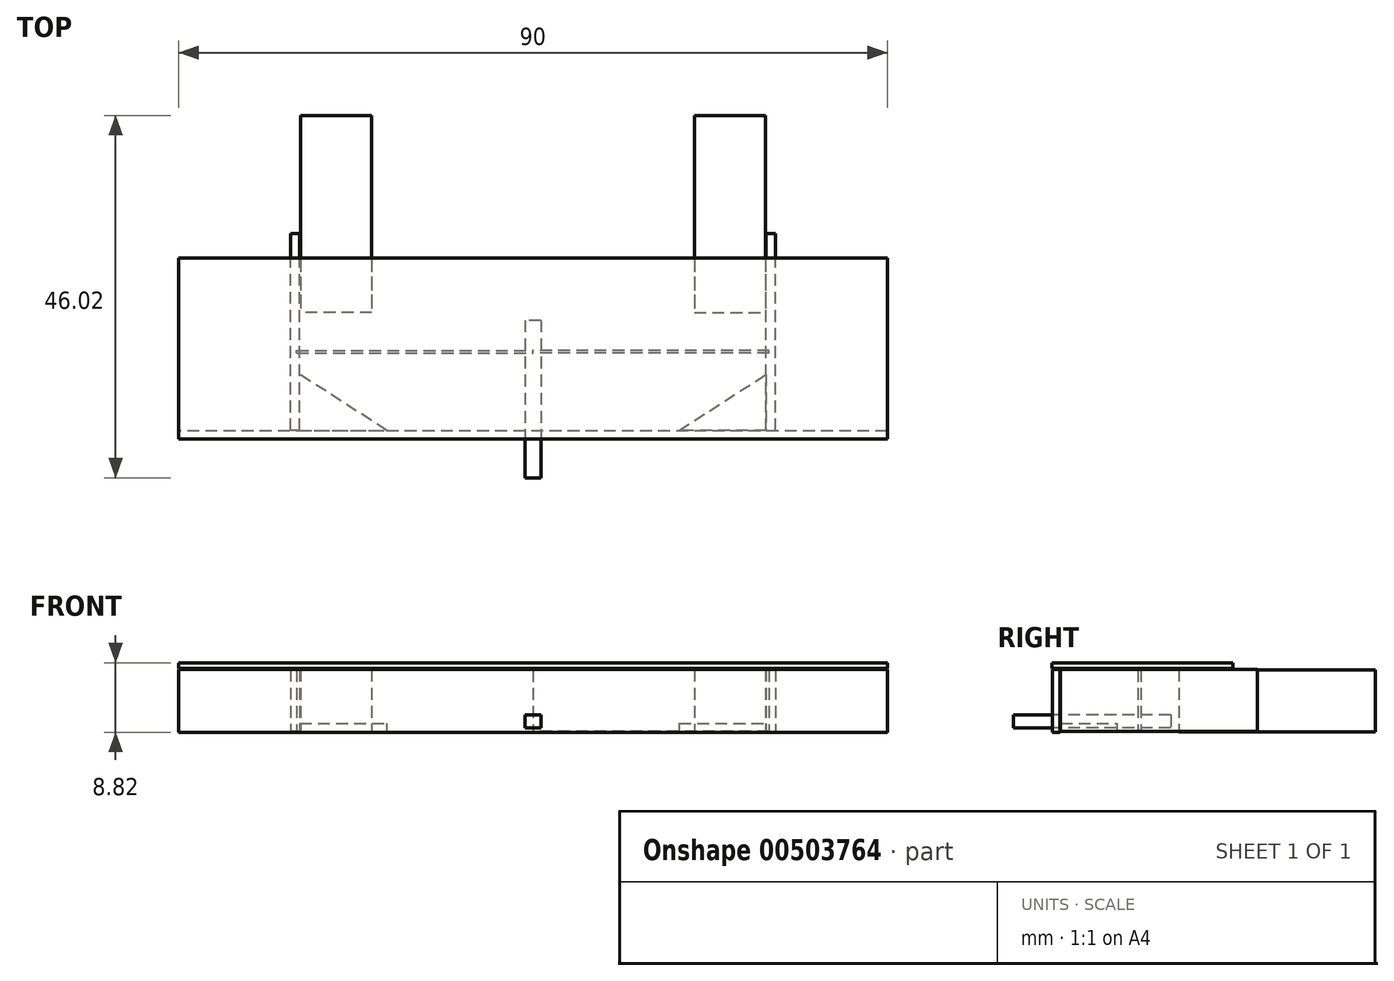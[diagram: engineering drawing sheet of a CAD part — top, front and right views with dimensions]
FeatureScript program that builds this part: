
annotation { "Feature Type Name" : "Feature", "Feature Type Description" : "" }
export const myFeature = defineFeature(function(context is Context, id is Id, definition is map)
    precondition{}
    {
        {
            var Q0;
            Q0=qCreatedBy(makeId("Front.planeOp"),FACE);
            var sketch = newSketch(context, id + "F0", { "sketchPlane" : qUnion([Q0])});
            skLineSegment(sketch, "E0.bottom", {"start": v(-20.5, 3.93) * mm, "end": v(-29.5, 3.93) * mm});
            skLineSegment(sketch, "E0.top", {"start": v(-20.5, -3.93) * mm, "end": v(-29.5, -3.93) * mm});
            skLineSegment(sketch, "E0.left", {"start": v(-20.5, 3.93) * mm, "end": v(-20.5, -3.93) * mm});
            skLineSegment(sketch, "E0.right", {"start": v(-29.5, 3.93) * mm, "end": v(-29.5, -3.93) * mm});
            skPoint(sketch, "E0.middle", {"position": v(-25, 0) * mm});
            skPoint(sketch, "E1.MirrorP", {"position": v(25, 0) * mm});
            skLineSegment(sketch, "E2.MirrorCS", {"start": v(20.5, 3.93) * mm, "end": v(20.5, -3.93) * mm});
            skLineSegment(sketch, "E3.MirrorCS", {"start": v(20.5, 3.93) * mm, "end": v(29.5, 3.93) * mm});
            skLineSegment(sketch, "E4.MirrorCS", {"start": v(29.5, 3.93) * mm, "end": v(29.5, -3.93) * mm});
            skLineSegment(sketch, "E5.MirrorCS", {"start": v(20.5, -3.93) * mm, "end": v(29.5, -3.93) * mm});
            skSolve(sketch);
        }
        {
            var Q0;
            Q0=makeQuery(id+"F0.imprint","IMPRINT",FACE,{"disambiguationData":[TD([[makeQuery(id+"F0.imprint","IMPRINT",EDGE,{"derivedFrom":sQuery(id+"F0.wireOp",EDGE,"E0.bottom")}),1.0]])]});
            var Q1;
            Q1=makeQuery(id+"F0.imprint","IMPRINT",FACE,{"disambiguationData":[TD([[makeQuery(id+"F0.imprint","IMPRINT",EDGE,{"derivedFrom":sQuery(id+"F0.wireOp",EDGE,"E2.MirrorCS")}),1.0]])]});
            extrude(context, id + "F1", {"entities" : qUnion([Q0, Q1]), "oppositeDirection" : true, "depth" : 25 * mm});
        }
        {
            var Q0;
            Q0=qCreatedBy(makeId("Front.planeOp"),FACE);
            var sketch = newSketch(context, id + "F2", { "sketchPlane" : qUnion([Q0])});
            skLineSegment(sketch, "E6.bottom", {"start": v(-29.62, 3.95) * mm, "end": v(-30.78, 3.95) * mm});
            skLineSegment(sketch, "E6.top", {"start": v(-29.62, -3.88) * mm, "end": v(-30.78, -3.88) * mm});
            skLineSegment(sketch, "E6.left", {"start": v(-29.62, 3.95) * mm, "end": v(-29.62, -3.88) * mm});
            skLineSegment(sketch, "E6.right", {"start": v(-30.78, 3.95) * mm, "end": v(-30.78, -3.88) * mm});
            skLineSegment(sketch, "E7.MirrorCS", {"start": v(29.62, 3.95) * mm, "end": v(29.62, -3.88) * mm});
            skLineSegment(sketch, "E8.MirrorCS", {"start": v(30.78, 3.95) * mm, "end": v(30.78, -3.88) * mm});
            skLineSegment(sketch, "E9.MirrorCS", {"start": v(29.62, -3.88) * mm, "end": v(30.78, -3.88) * mm});
            skLineSegment(sketch, "E10.MirrorCS", {"start": v(29.62, 3.95) * mm, "end": v(30.78, 3.95) * mm});
            skSolve(sketch);
        }
        {
            var Q0;
            Q0 = qSketchRegion(id + "F2", true);
            extrude(context, id + "F3", {"entities" : qUnion([Q0]), "depth" : 15 * mm});
        }
        {
            var Q0;
            Q0=makeQuery(id+"F3.opExtrude","CAP_FACE",FACE,{"disambiguationData":[OSD([sQuery(id+"F2.wireOp",EDGE,"E6.bottom"),sQuery(id+"F2.wireOp",EDGE,"E6.top"),sQuery(id+"F2.wireOp",EDGE,"E6.left"),sQuery(id+"F2.wireOp",EDGE,"E6.right")])],"isStart":true});
            extrude(context, id + "F4", {"entities" : qUnion([Q0]), "operationType" : NewBodyOperationType.ADD, "depth" : 10 * mm});
        }
        {
            var Q0;
            Q0=makeQuery(id+"F3.opExtrude","CAP_FACE",FACE,{"disambiguationData":[OSD([sQuery(id+"F2.wireOp",EDGE,"E7.MirrorCS"),sQuery(id+"F2.wireOp",EDGE,"E8.MirrorCS"),sQuery(id+"F2.wireOp",EDGE,"E9.MirrorCS"),sQuery(id+"F2.wireOp",EDGE,"E10.MirrorCS")])],"isStart":true});
            extrude(context, id + "F5", {"entities" : qUnion([Q0]), "operationType" : NewBodyOperationType.ADD, "depth" : 10 * mm});
        }
        {
            var Q0;
            Q0=qCreatedBy(makeId("Right.planeOp"),FACE);
            var sketch = newSketch(context, id + "F6", { "sketchPlane" : qUnion([Q0])});
            skLineSegment(sketch, "E11.bottom", {"start": v(-15.08, 3.97) * mm, "end": v(-16.02, 3.97) * mm});
            skLineSegment(sketch, "E11.top", {"start": v(-15.08, -4) * mm, "end": v(-16.02, -4) * mm});
            skLineSegment(sketch, "E11.left", {"start": v(-15.08, 3.97) * mm, "end": v(-15.08, -4) * mm});
            skLineSegment(sketch, "E11.right", {"start": v(-16.02, 3.97) * mm, "end": v(-16.02, -4) * mm});
            skSolve(sketch);
        }
        {
            var Q0;
            Q0=makeQuery(id+"F6.imprint","IMPRINT",FACE,{"disambiguationData":[TD([[makeQuery(id+"F6.imprint","IMPRINT",EDGE,{"derivedFrom":sQuery(id+"F6.wireOp",EDGE,"E11.bottom")}),1.0]])]});
            extrude(context, id + "F7", {"entities" : qUnion([Q0]), "depth" : 45 * mm});
        }
        {
            var Q0;
            Q0=makeQuery(id+"F7.opExtrude","CAP_FACE",FACE,{"disambiguationData":[OSD([sQuery(id+"F6.wireOp",EDGE,"E11.bottom"),sQuery(id+"F6.wireOp",EDGE,"E11.top"),sQuery(id+"F6.wireOp",EDGE,"E11.left"),sQuery(id+"F6.wireOp",EDGE,"E11.right")])],"isStart":true});
            extrude(context, id + "F8", {"entities" : qUnion([Q0]), "operationType" : NewBodyOperationType.ADD, "depth" : 45 * mm});
        }
        {
            var Q0;
            Q0=qCreatedBy(makeId("Right.planeOp"),FACE);
            var sketch = newSketch(context, id + "F9", { "sketchPlane" : qUnion([Q0])});
            skLineSegment(sketch, "E12.bottom", {"start": v(-16.1, 4.1) * mm, "end": v(6.88, 4.1) * mm});
            skLineSegment(sketch, "E12.top", {"start": v(-16.1, 4.81) * mm, "end": v(6.88, 4.81) * mm});
            skLineSegment(sketch, "E12.left", {"start": v(-16.1, 4.1) * mm, "end": v(-16.1, 4.81) * mm});
            skLineSegment(sketch, "E12.right", {"start": v(6.88, 4.1) * mm, "end": v(6.88, 4.81) * mm});
            skSolve(sketch);
        }
        {
            var Q0;
            Q0 = qSketchRegion(id + "F9", true);
            extrude(context, id + "F10", {"entities" : qUnion([Q0]), "depth" : 45 * mm});
        }
        {
            var Q0;
            Q0=makeQuery(id+"F10.opExtrude","CAP_FACE",FACE,{"disambiguationData":[OSD([sQuery(id+"F9.wireOp",EDGE,"E12.bottom"),sQuery(id+"F9.wireOp",EDGE,"E12.top"),sQuery(id+"F9.wireOp",EDGE,"E12.left"),sQuery(id+"F9.wireOp",EDGE,"E12.right")])],"isStart":true});
            extrude(context, id + "F11", {"entities" : qUnion([Q0]), "operationType" : NewBodyOperationType.ADD, "depth" : 45 * mm});
        }
        {
            var Q0;
            {var subQ0=sQuery(id+"F2.wireOp",EDGE,"E6.top");Q0=makeQuery(id+"F4.boolean.opBoolean","MERGE",FACE,{"derivedFrom":[makeQuery(id+"F3.opExtrude","SWEPT_FACE",FACE,{"disambiguationData":[OSD([subQ0])]}),makeQuery(id+"F4.opExtrude","SWEPT_FACE",FACE,{"disambiguationData":[OSD([subQ0])]})]});}
            var sketch = newSketch(context, id + "F12", { "sketchPlane" : qUnion([Q0])});
            skLineSegment(sketch, "E13", {"start": v(-29.62, 15) * mm, "end": v(-18.58, 15) * mm});
            skLineSegment(sketch, "E14", {"start": v(-18.58, 15) * mm, "end": v(-29.62, 7.86) * mm});
            skLineSegment(sketch, "E15", {"start": v(-29.62, 7.86) * mm, "end": v(-29.62, 15) * mm});
            skLineSegment(sketch, "E16.MirrorCS", {"start": v(29.62, 7.86) * mm, "end": v(29.62, 15) * mm});
            skLineSegment(sketch, "E17.MirrorCS", {"start": v(18.58, 15) * mm, "end": v(29.62, 7.86) * mm});
            skLineSegment(sketch, "E18.MirrorCS", {"start": v(29.62, 15) * mm, "end": v(18.58, 15) * mm});
            skSolve(sketch);
        }
        {
            var Q0;
            Q0=makeQuery(id+"F12.imprint","IMPRINT",FACE,{"disambiguationData":[TD([[makeQuery(id+"F12.imprint","IMPRINT",EDGE,{"derivedFrom":sQuery(id+"F12.wireOp",EDGE,"E13")}),-1.0]])]});
            var Q1;
            Q1=makeQuery(id+"F12.imprint","IMPRINT",FACE,{"disambiguationData":[TD([[makeQuery(id+"F12.imprint","IMPRINT",EDGE,{"derivedFrom":sQuery(id+"F12.wireOp",EDGE,"E17.MirrorCS")}),1.0]])]});
            extrude(context, id + "F13", {"entities" : qUnion([Q0, Q1]), "oppositeDirection" : true, "depth" : 1 * mm});
        }
        {
            var Q0;
            Q0=qCreatedBy(makeId("Right.planeOp"),FACE);
            var sketch = newSketch(context, id + "F14", { "sketchPlane" : qUnion([Q0])});
            skLineSegment(sketch, "E19.bottom", {"start": v(-0.18, 3.91) * mm, "end": v(0.18, 3.91) * mm});
            skLineSegment(sketch, "E19.top", {"start": v(-0.18, -3.91) * mm, "end": v(0.18, -3.91) * mm});
            skLineSegment(sketch, "E19.left", {"start": v(-0.18, 3.91) * mm, "end": v(-0.18, -3.91) * mm});
            skLineSegment(sketch, "E19.right", {"start": v(0.18, 3.91) * mm, "end": v(0.18, -3.91) * mm});
            skPoint(sketch, "E19.middle", {"position": v(0, 0) * mm});
            skSolve(sketch);
        }
        {
            var Q0;
            Q0 = qSketchRegion(id + "F14", true);
            extrude(context, id + "F15", {"entities" : qUnion([Q0]), "depth" : 30 * mm});
        }
        {
            var Q0;
            Q0=makeQuery(id+"F15.opExtrude","CAP_FACE",FACE,{"disambiguationData":[OSD([sQuery(id+"F14.wireOp",EDGE,"E19.bottom"),sQuery(id+"F14.wireOp",EDGE,"E19.top"),sQuery(id+"F14.wireOp",EDGE,"E19.left"),sQuery(id+"F14.wireOp",EDGE,"E19.right")])],"isStart":true});
            extrude(context, id + "F16", {"entities" : qUnion([Q0]), "depth" : 30 * mm});
        }
        {
            var Q0;
            Q0=makeQuery(id+"F16.opExtrude","SWEPT_BODY",BODY,{"disambiguationData":[OSD([sQuery(id+"F14.wireOp",EDGE,"E19.bottom"),sQuery(id+"F14.wireOp",EDGE,"E19.top"),sQuery(id+"F14.wireOp",EDGE,"E19.left"),sQuery(id+"F14.wireOp",EDGE,"E19.right")])]});
            var Q1;
            Q1=makeQuery(id+"F15.opExtrude","SWEPT_BODY",BODY,{"disambiguationData":[OSD([sQuery(id+"F14.wireOp",EDGE,"E19.bottom"),sQuery(id+"F14.wireOp",EDGE,"E19.top"),sQuery(id+"F14.wireOp",EDGE,"E19.left"),sQuery(id+"F14.wireOp",EDGE,"E19.right")])]});
            transform(context, id + "F17", {"entities" : qUnion([Q0, Q1]), "transformType" : TransformType.TRANSLATION_3D, "dx" : 0 * mm, "dy" : -5 * mm, "dz" : 0 * mm, "makeCopy" : false});
        }
        {
            var Q0;
            {var subQ0=sQuery(id+"F6.wireOp",EDGE,"E11.right");Q0=makeQuery(id+"F8.boolean.opBoolean","MERGE",FACE,{"derivedFrom":[makeQuery(id+"F7.opExtrude","SWEPT_FACE",FACE,{"disambiguationData":[OSD([subQ0])]}),makeQuery(id+"F8.opExtrude","SWEPT_FACE",FACE,{"disambiguationData":[OSD([subQ0])]})]});}
            var sketch = newSketch(context, id + "F18", { "sketchPlane" : qUnion([Q0])});
            skLineSegment(sketch, "E20.bottom", {"start": v(1, -1.8) * mm, "end": v(-1, -1.8) * mm});
            skLineSegment(sketch, "E20.top", {"start": v(1, -3.48) * mm, "end": v(-1, -3.48) * mm});
            skLineSegment(sketch, "E20.left", {"start": v(1, -1.8) * mm, "end": v(1, -3.48) * mm});
            skLineSegment(sketch, "E20.right", {"start": v(-1, -1.8) * mm, "end": v(-1, -3.48) * mm});
            skPoint(sketch, "E20.middle", {"position": v(0, -2.64) * mm});
            skSolve(sketch);
        }
        {
            var Q0;
            Q0 = qSketchRegion(id + "F18", true);
            extrude(context, id + "F19", {"entities" : qUnion([Q0]), "oppositeDirection" : true, "depth" : 15 * mm});
        }
        {
            var Q0;
            Q0=makeQuery(id+"F19.opExtrude","CAP_FACE",FACE,{"disambiguationData":[OSD([sQuery(id+"F18.wireOp",EDGE,"E20.bottom"),sQuery(id+"F18.wireOp",EDGE,"E20.top"),sQuery(id+"F18.wireOp",EDGE,"E20.left"),sQuery(id+"F18.wireOp",EDGE,"E20.right")])],"isStart":true});
            extrude(context, id + "F20", {"entities" : qUnion([Q0]), "depth" : 5 * mm});
        }
    });
